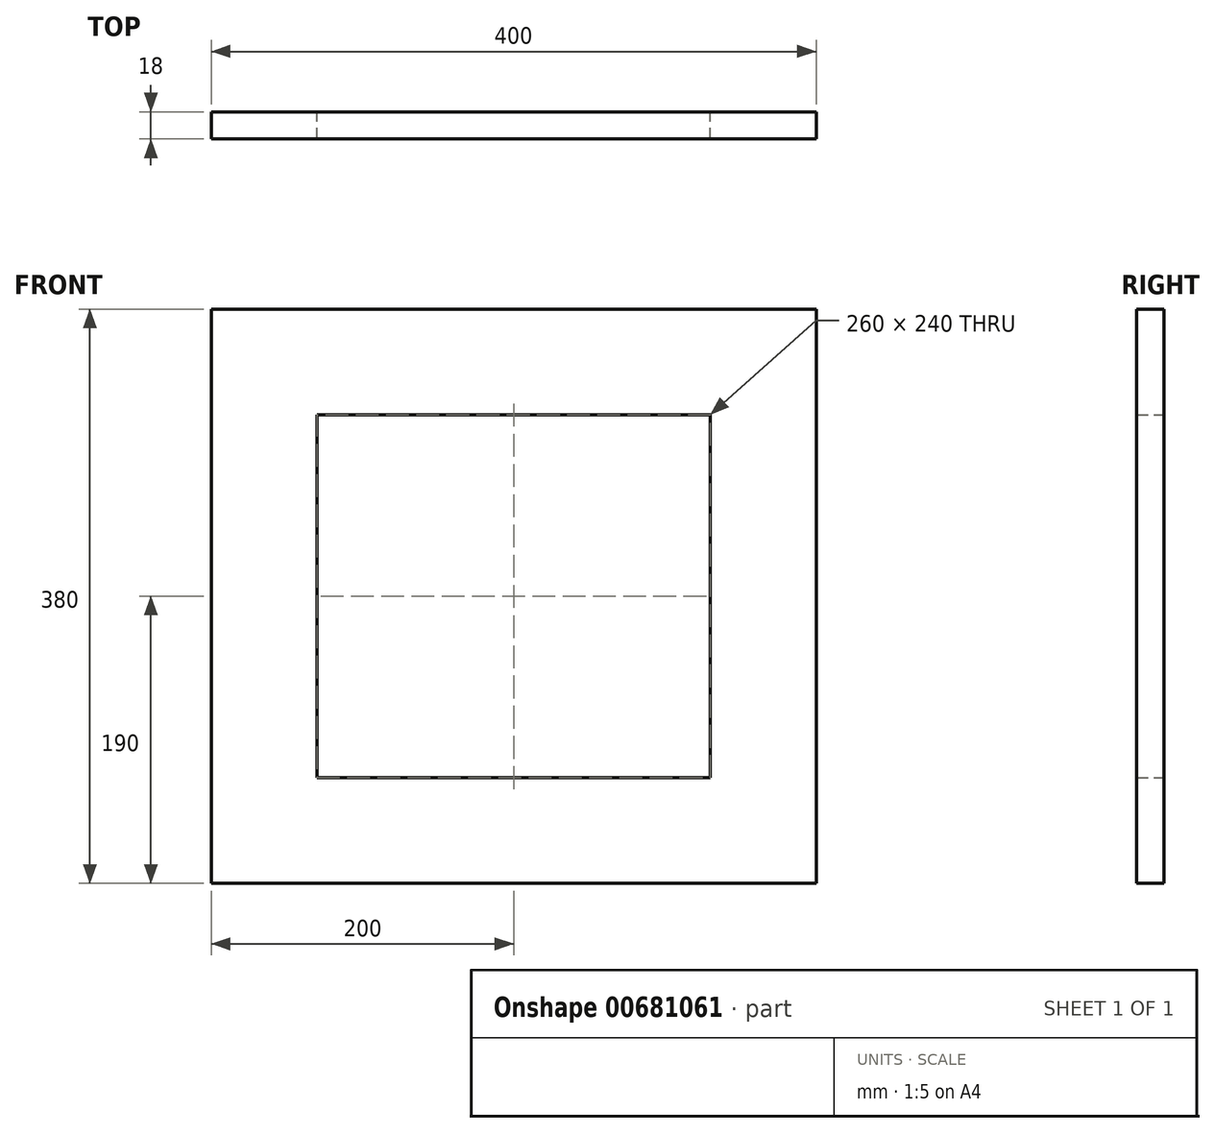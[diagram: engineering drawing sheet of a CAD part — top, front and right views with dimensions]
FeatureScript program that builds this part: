
annotation { "Feature Type Name" : "Feature", "Feature Type Description" : "" }
export const myFeature = defineFeature(function(context is Context, id is Id, definition is map)
    precondition{}
    {
        {
            var Q0;
            Q0=qCreatedBy(makeId("Front.planeOp"),FACE);
            var sketch = newSketch(context, id + "F0", { "sketchPlane" : qUnion([Q0])});
            skLineSegment(sketch, "E0.bottom", {"start": v(-70, 380) * mm, "end": v(0, 380) * mm});
            skLineSegment(sketch, "E0.top", {"start": v(-70, 0) * mm, "end": v(0, 0) * mm});
            skLineSegment(sketch, "E0.left", {"start": v(-70, 380) * mm, "end": v(-70, 0) * mm});
            skLineSegment(sketch, "E0.right", {"start": v(0, 380) * mm, "end": v(0, 0) * mm});
            skLineSegment(sketch, "E1.bottom", {"start": v(260, 380) * mm, "end": v(330, 380) * mm});
            skLineSegment(sketch, "E1.top", {"start": v(260, 0) * mm, "end": v(330, 0) * mm});
            skLineSegment(sketch, "E1.left", {"start": v(260, 380) * mm, "end": v(260, 0) * mm});
            skLineSegment(sketch, "E1.right", {"start": v(330, 380) * mm, "end": v(330, 0) * mm});
            skLineSegment(sketch, "E2.bottom", {"start": v(0, 0) * mm, "end": v(260, 0) * mm});
            skLineSegment(sketch, "E2.top", {"start": v(0, 70) * mm, "end": v(260, 70) * mm});
            skLineSegment(sketch, "E2.left", {"start": v(0, 0) * mm, "end": v(0, 70) * mm});
            skLineSegment(sketch, "E2.right", {"start": v(260, 0) * mm, "end": v(260, 70) * mm});
            skLineSegment(sketch, "E3.bottom", {"start": v(0, 380) * mm, "end": v(260, 380) * mm});
            skLineSegment(sketch, "E3.top", {"start": v(0, 310) * mm, "end": v(260, 310) * mm});
            skLineSegment(sketch, "E3.left", {"start": v(0, 380) * mm, "end": v(0, 310) * mm});
            skLineSegment(sketch, "E3.right", {"start": v(260, 380) * mm, "end": v(260, 310) * mm});
            skSolve(sketch);
        }
        {
            var Q0;
            Q0=makeQuery(id+"F0.imprint","IMPRINT",FACE,{"disambiguationData":[TD([[makeQuery(id+"F0.imprint","IMPRINT",EDGE,{"derivedFrom":sQuery(id+"F0.wireOp",EDGE,"E0.bottom")}),-1.0]])]});
            var Q1;
            Q1=makeQuery(id+"F0.imprint","IMPRINT",FACE,{"disambiguationData":[TD([[makeQuery(id+"F0.imprint","IMPRINT",EDGE,{"derivedFrom":sQuery(id+"F0.wireOp",EDGE,"E3.bottom")}),-1.0]])]});
            var Q2;
            Q2=makeQuery(id+"F0.imprint","IMPRINT",FACE,{"disambiguationData":[TD([[makeQuery(id+"F0.imprint","IMPRINT",EDGE,{"derivedFrom":sQuery(id+"F0.wireOp",EDGE,"E1.bottom")}),-1.0]])]});
            var Q3;
            Q3=makeQuery(id+"F0.imprint","IMPRINT",FACE,{"disambiguationData":[TD([[makeQuery(id+"F0.imprint","IMPRINT",EDGE,{"derivedFrom":sQuery(id+"F0.wireOp",EDGE,"E2.bottom")}),1.0]])]});
            extrude(context, id + "F1", {"entities" : qUnion([Q0, Q1, Q2, Q3]), "depth" : 18 * mm, "offsetDistance" : 25 * mm});
        }
    });
